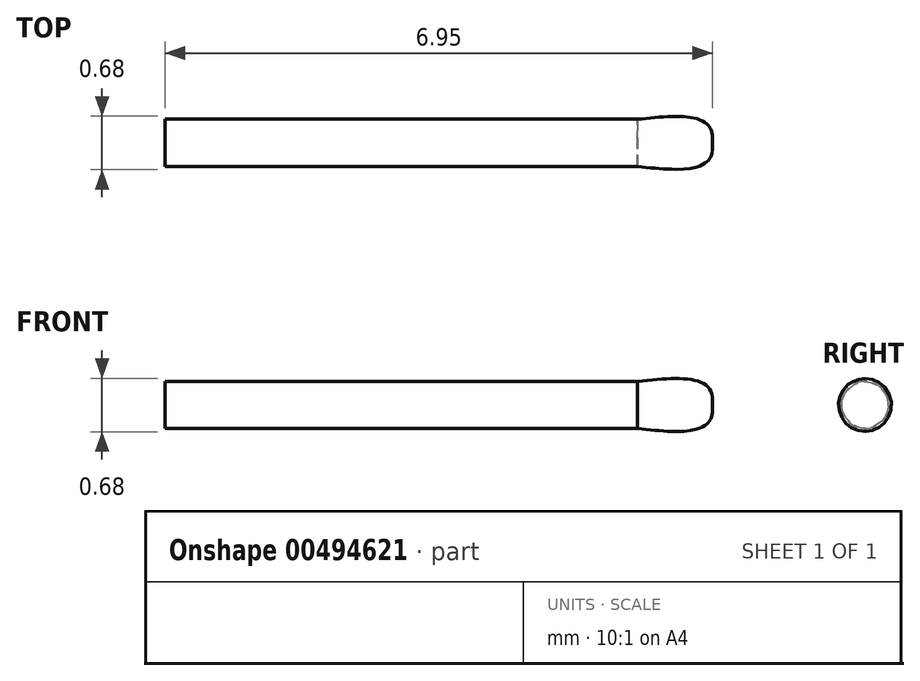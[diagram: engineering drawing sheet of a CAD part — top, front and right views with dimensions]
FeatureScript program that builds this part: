
annotation { "Feature Type Name" : "Feature", "Feature Type Description" : "" }
export const myFeature = defineFeature(function(context is Context, id is Id, definition is map)
    precondition{}
    {
        {
            var Q0;
            Q0=qCreatedBy(makeId("Right.planeOp"),FACE);
            var sketch = newSketch(context, id + "F0", { "sketchPlane" : qUnion([Q0])});
            skCircle(sketch, "E0", {"center": v(0, 0) * mm, "radius": 0.3 * mm});
            skSolve(sketch);
        }
        {
            var Q0;
            Q0=makeQuery(id+"F0.imprint","IMPRINT",FACE,{"disambiguationData":[TD([[makeQuery(id+"F0.imprint","IMPRINT",EDGE,{"derivedFrom":sQuery(id+"F0.wireOp",EDGE,"E0")}),1.0]])]});
            extrude(context, id + "F1", {"entities" : qUnion([Q0]), "depth" : 6 * mm, "offsetDistance" : 25 * mm});
        }
        {
            var Q0;
            Q0=makeQuery(id+"F1.opExtrude","CAP_FACE",FACE,{"disambiguationData":[OSD([sQuery(id+"F0.wireOp",EDGE,"E0")])],"isStart":false});
            var sketch = newSketch(context, id + "F2", { "sketchPlane" : qUnion([Q0])});
            skCircle(sketch, "E1", {"center": v(0, 0) * mm, "radius": 0.47 * mm});
            skSolve(sketch);
        }
        {
            var Q0;
            Q0=qCreatedBy(makeId("Right.planeOp"),FACE);
            cPlane(context, id + "F3", {"entities" : qUnion([Q0]), "cplaneType" : CPlaneType.OFFSET, "offset" : 6.95 * mm, "width" : 150 * mm, "height" : 150 * mm});
        }
        {
            var Q0;
            Q0=qCreatedBy(id+"F3.planeOp",FACE);
            var sketch = newSketch(context, id + "F4", { "sketchPlane" : qUnion([Q0])});
            skCircle(sketch, "E2", {"center": v(0, 0) * mm, "radius": 0.1 * mm});
            skSolve(sketch);
        }
        {
            var Q0;
            Q0=sQuery(id+"F4.wireOp",VERTEX,"E2.center");
            var Q1;
            Q1=makeQuery(id+"F4.imprint","IMPRINT",FACE,{"disambiguationData":[TD([[makeQuery(id+"F4.imprint","IMPRINT",EDGE,{"derivedFrom":sQuery(id+"F4.wireOp",EDGE,"E2")}),1.0]])]});
            var Q2;
            Q2=makeQuery(id+"F2.imprint","IMPRINT",FACE,{"disambiguationData":[TD([[makeQuery(id+"F2.imprint","IMPRINT",EDGE,{"derivedFrom":makeQuery(id+"F1.opExtrude","CAP_EDGE",EDGE,{"disambiguationData":[OSD([sQuery(id+"F0.wireOp",EDGE,"E0")])],"isStart":false})}),1.0]])]});
            loft(context, id + "F5", {"operationType" : NewBodyOperationType.ADD, "sheetProfilesArray" : [{ "sheetProfileEntities" : qUnion([Q0]) }, { "sheetProfileEntities" : qUnion([Q1]) }, { "sheetProfileEntities" : qUnion([Q2]) }]});
        }
    });
